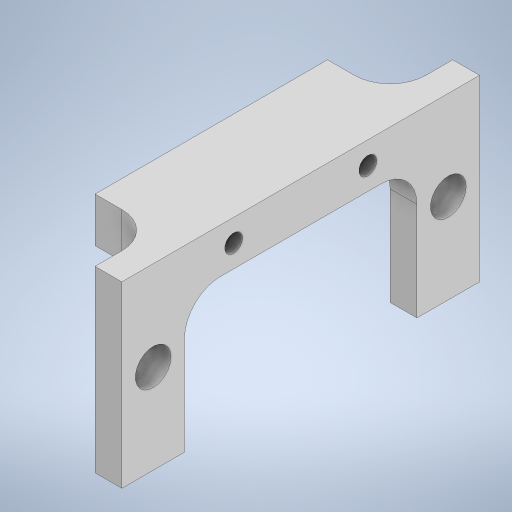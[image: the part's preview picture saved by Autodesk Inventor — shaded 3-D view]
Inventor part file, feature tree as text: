
AUTODESK INVENTOR PART (.ipt)
format: ipt  version: 2024.2 (Build 282272000, 272)  size: 270,848 bytes
history: native  units: mm
features: extrude x3, sketch x3, fillet x2
ambient origin geometry x8: Origin, YZ Plane, XZ Plane, XY Plane, X Axis, Y Axis, Z Axis, Center Point
bodies: Solid1 (feature_tree)
feature tree (8):
  extrude  "Extrusion1"  Depth=10.0mm
  extrude  "Extrusion2"  Depth=7.0mm
  extrude  "Extrusion3"  Depth=2.0mm
  fillet  "Fillet1"  Radius=20.0mm
  fillet  "Fillet2"  Radius=15.0mm
  sketch  "Sketch1"  dims[d0=10.0mm d1=40.0mm]
  sketch  "Sketch2"  dims[d2=7.0mm d3=7.0mm]
  sketch  "Sketch3"  dims[d4=7.0mm d5=7.0mm d6=20.0mm d7=0.0mm d8=15.0mm d9=4.0mm d10=4.0mm d11=0.0mm d12=0.0mm d13=2.0mm d14=2.0mm d15=15.0mm d16=0.0mm d17=0.0mm d18=4.0mm d19=2.0mm]
